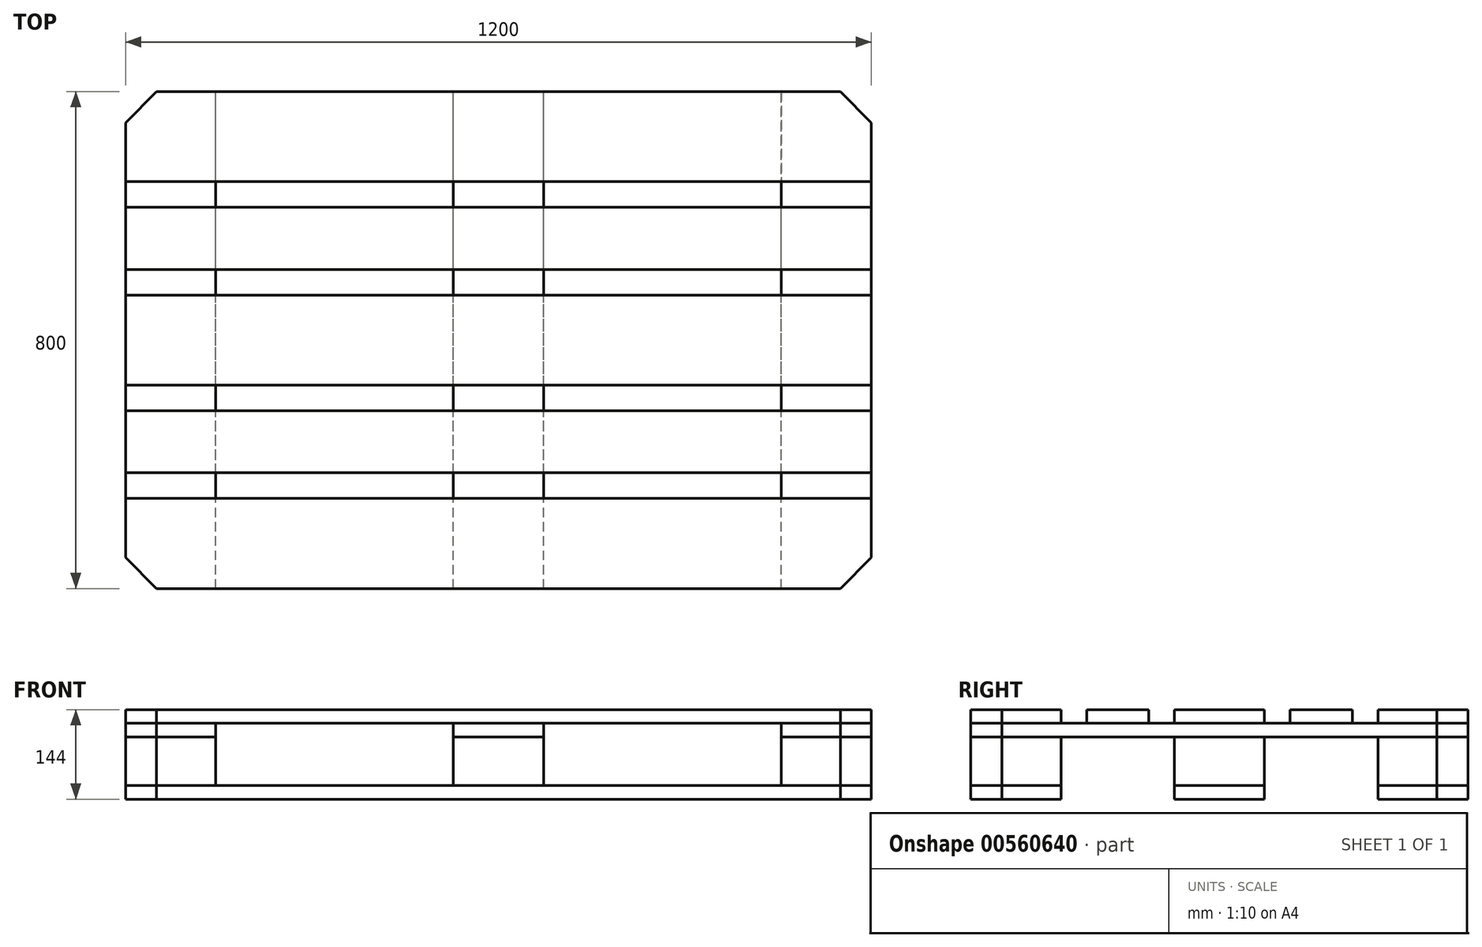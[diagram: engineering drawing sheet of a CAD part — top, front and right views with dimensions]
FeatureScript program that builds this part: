
annotation { "Feature Type Name" : "Feature", "Feature Type Description" : "" }
export const myFeature = defineFeature(function(context is Context, id is Id, definition is map)
    precondition{}
    {
        {
            var Q0;
            Q0=qCreatedBy(makeId("Top.planeOp"),FACE);
            var sketch = newSketch(context, id + "F0", { "sketchPlane" : qUnion([Q0])});
            skLineSegment(sketch, "E0.bottom", {"start": v(600, -72.5) * mm, "end": v(-600, -72.5) * mm});
            skLineSegment(sketch, "E0.top", {"start": v(600, 72.5) * mm, "end": v(-600, 72.5) * mm});
            skLineSegment(sketch, "E0.left", {"start": v(600, -72.5) * mm, "end": v(600, 72.5) * mm});
            skLineSegment(sketch, "E0.right", {"start": v(-600, -72.5) * mm, "end": v(-600, 72.5) * mm});
            skPoint(sketch, "E0.middle", {"position": v(0, 0) * mm});
            skLineSegment(sketch, "E1.bottom", {"start": v(600, -213.75) * mm, "end": v(-600, -213.75) * mm});
            skLineSegment(sketch, "E1.top", {"start": v(600, -113.75) * mm, "end": v(-600, -113.75) * mm});
            skLineSegment(sketch, "E1.left", {"start": v(600, -213.75) * mm, "end": v(600, -113.75) * mm});
            skLineSegment(sketch, "E1.right", {"start": v(-600, -213.75) * mm, "end": v(-600, -113.75) * mm});
            skPoint(sketch, "E1.middle", {"position": v(0, -163.75) * mm});
            skLineSegment(sketch, "E2.bottom", {"start": v(600, -400) * mm, "end": v(-600, -400) * mm});
            skLineSegment(sketch, "E2.top", {"start": v(600, -255) * mm, "end": v(-600, -255) * mm});
            skLineSegment(sketch, "E2.left", {"start": v(600, -400) * mm, "end": v(600, -255) * mm});
            skLineSegment(sketch, "E2.right", {"start": v(-600, -400) * mm, "end": v(-600, -255) * mm});
            skPoint(sketch, "E2.middle", {"position": v(0, -327.5) * mm});
            skLineSegment(sketch, "E3.bottom", {"start": v(-600, 213.75) * mm, "end": v(600, 213.75) * mm});
            skLineSegment(sketch, "E3.top", {"start": v(-600, 113.75) * mm, "end": v(600, 113.75) * mm});
            skLineSegment(sketch, "E3.left", {"start": v(-600, 213.75) * mm, "end": v(-600, 113.75) * mm});
            skLineSegment(sketch, "E3.right", {"start": v(600, 213.75) * mm, "end": v(600, 113.75) * mm});
            skPoint(sketch, "E3.middle", {"position": v(0, 163.75) * mm});
            skLineSegment(sketch, "E4.bottom", {"start": v(-600, 400) * mm, "end": v(600, 400) * mm});
            skLineSegment(sketch, "E4.top", {"start": v(-600, 255) * mm, "end": v(600, 255) * mm});
            skLineSegment(sketch, "E4.left", {"start": v(-600, 400) * mm, "end": v(-600, 255) * mm});
            skLineSegment(sketch, "E4.right", {"start": v(600, 400) * mm, "end": v(600, 255) * mm});
            skPoint(sketch, "E4.middle", {"position": v(0, 327.5) * mm});
            skLineSegment(sketch, "E5", {"start": v(-600, 163.75) * mm, "end": v(600, 163.75) * mm, "construction": true});
            skSolve(sketch);
        }
        {
            var Q0;
            Q0=makeQuery(id+"F0.imprint","IMPRINT",FACE,{"disambiguationData":[TD([[makeQuery(id+"F0.imprint","IMPRINT",EDGE,{"derivedFrom":sQuery(id+"F0.wireOp",EDGE,"E4.bottom")}),-1.0]])]});
            var Q1;
            Q1=makeQuery(id+"F0.imprint","IMPRINT",FACE,{"disambiguationData":[TD([[makeQuery(id+"F0.imprint","IMPRINT",EDGE,{"derivedFrom":sQuery(id+"F0.wireOp",EDGE,"E3.bottom")}),-1.0]])]});
            var Q2;
            Q2=makeQuery(id+"F0.imprint","IMPRINT",FACE,{"disambiguationData":[TD([[makeQuery(id+"F0.imprint","IMPRINT",EDGE,{"derivedFrom":sQuery(id+"F0.wireOp",EDGE,"E0.bottom")}),-1.0]])]});
            var Q3;
            Q3=makeQuery(id+"F0.imprint","IMPRINT",FACE,{"disambiguationData":[TD([[makeQuery(id+"F0.imprint","IMPRINT",EDGE,{"derivedFrom":sQuery(id+"F0.wireOp",EDGE,"E1.bottom")}),-1.0]])]});
            var Q4;
            Q4=makeQuery(id+"F0.imprint","IMPRINT",FACE,{"disambiguationData":[TD([[makeQuery(id+"F0.imprint","IMPRINT",EDGE,{"derivedFrom":sQuery(id+"F0.wireOp",EDGE,"E2.bottom")}),-1.0]])]});
            extrude(context, id + "F1", {"entities" : qUnion([Q0, Q1, Q2, Q3, Q4]), "oppositeDirection" : true, "depth" : 22 * mm, "offsetDistance" : 25 * mm});
        }
        {
            var Q0;
            Q0=makeQuery(id+"F1.opExtrude","CAP_FACE",FACE,{"disambiguationData":[OSD([sQuery(id+"F0.wireOp",EDGE,"E2.bottom"),sQuery(id+"F0.wireOp",EDGE,"E2.top"),sQuery(id+"F0.wireOp",EDGE,"E2.left"),sQuery(id+"F0.wireOp",EDGE,"E2.right")])],"isStart":false});
            var sketch = newSketch(context, id + "F2", { "sketchPlane" : qUnion([Q0])});
            skLineSegment(sketch, "E6.bottom", {"start": v(-600, 400) * mm, "end": v(-455, 400) * mm});
            skLineSegment(sketch, "E6.top", {"start": v(-600, -400) * mm, "end": v(-455, -400) * mm});
            skLineSegment(sketch, "E6.left", {"start": v(-600, 400) * mm, "end": v(-600, -400) * mm});
            skLineSegment(sketch, "E6.right", {"start": v(-455, 400) * mm, "end": v(-455, -400) * mm});
            skLineSegment(sketch, "E7.bottom", {"start": v(-72.5, 400) * mm, "end": v(72.5, 400) * mm});
            skLineSegment(sketch, "E7.top", {"start": v(-72.5, -400) * mm, "end": v(72.5, -400) * mm});
            skLineSegment(sketch, "E7.left", {"start": v(-72.5, 400) * mm, "end": v(-72.5, -400) * mm});
            skLineSegment(sketch, "E7.right", {"start": v(72.5, 400) * mm, "end": v(72.5, -400) * mm});
            skLineSegment(sketch, "E8.bottom", {"start": v(600, 400) * mm, "end": v(455, 400) * mm});
            skLineSegment(sketch, "E8.top", {"start": v(600, -400) * mm, "end": v(455, -400) * mm});
            skLineSegment(sketch, "E8.left", {"start": v(600, 400) * mm, "end": v(600, -400) * mm});
            skLineSegment(sketch, "E8.right", {"start": v(455, 400) * mm, "end": v(455, -400) * mm});
            skSolve(sketch);
        }
        {
            var Q0;
            {var subQ0=sQuery(id+"F2.wireOp",EDGE,"E6.top");Q0=makeQuery(id+"F2.imprint","IMPRINT",FACE,{"disambiguationData":[TD([[makeQuery(id+"F2.imprint","IMPRINT",EDGE,{"derivedFrom":subQ0}),1.0]])]});}
            var Q1;
            {var subQ0=sQuery(id+"F2.wireOp",EDGE,"E6.bottom");Q1=makeQuery(id+"F2.imprint","IMPRINT",FACE,{"disambiguationData":[TD([[makeQuery(id+"F2.imprint","IMPRINT",EDGE,{"derivedFrom":subQ0}),1.0]])]});}
            var Q2;
            {var subQ0=sQuery(id+"F2.wireOp",EDGE,"E7.bottom");Q2=makeQuery(id+"F2.imprint","IMPRINT",FACE,{"disambiguationData":[TD([[makeQuery(id+"F2.imprint","IMPRINT",EDGE,{"derivedFrom":subQ0}),1.0]])]});}
            var Q3;
            {var subQ0=sQuery(id+"F2.wireOp",EDGE,"E7.top");Q3=makeQuery(id+"F2.imprint","IMPRINT",FACE,{"disambiguationData":[TD([[makeQuery(id+"F2.imprint","IMPRINT",EDGE,{"derivedFrom":subQ0}),1.0]])]});}
            var Q4;
            {var subQ0=sQuery(id+"F2.wireOp",EDGE,"E8.bottom");Q4=makeQuery(id+"F2.imprint","IMPRINT",FACE,{"disambiguationData":[TD([[makeQuery(id+"F2.imprint","IMPRINT",EDGE,{"derivedFrom":subQ0}),1.0]])]});}
            var Q5;
            {var subQ0=sQuery(id+"F2.wireOp",EDGE,"E8.top");Q5=makeQuery(id+"F2.imprint","IMPRINT",FACE,{"disambiguationData":[TD([[makeQuery(id+"F2.imprint","IMPRINT",EDGE,{"derivedFrom":subQ0}),-1.0]])]});}
            extrude(context, id + "F3", {"entities" : qUnion([Q0, Q1, Q2, Q3, Q4, Q5]), "depth" : 22 * mm, "offsetDistance" : 25 * mm});
        }
        {
            var Q0;
            Q0=makeQuery(id+"F3.opExtrude","CAP_FACE",FACE,{"disambiguationData":[OSD([sQuery(id+"F2.wireOp",EDGE,"E6.bottom"),sQuery(id+"F2.wireOp",EDGE,"E6.top"),sQuery(id+"F2.wireOp",EDGE,"E6.left"),sQuery(id+"F2.wireOp",EDGE,"E6.right")])],"isStart":false});
            var sketch = newSketch(context, id + "F4", { "sketchPlane" : qUnion([Q0])});
            skLineSegment(sketch, "E9.bottom", {"start": v(-600, 400) * mm, "end": v(-455, 400) * mm});
            skLineSegment(sketch, "E9.top", {"start": v(-600, 255) * mm, "end": v(-455, 255) * mm});
            skLineSegment(sketch, "E9.left", {"start": v(-600, 400) * mm, "end": v(-600, 255) * mm});
            skLineSegment(sketch, "E9.right", {"start": v(-455, 400) * mm, "end": v(-455, 255) * mm});
            skLineSegment(sketch, "E10.bottom", {"start": v(-600, 72.5) * mm, "end": v(-455, 72.5) * mm});
            skLineSegment(sketch, "E10.top", {"start": v(-600, -72.5) * mm, "end": v(-455, -72.5) * mm});
            skLineSegment(sketch, "E10.left", {"start": v(-600, 72.5) * mm, "end": v(-600, -72.5) * mm});
            skLineSegment(sketch, "E10.right", {"start": v(-455, 72.5) * mm, "end": v(-455, -72.5) * mm});
            skLineSegment(sketch, "E11.bottom", {"start": v(-600, -400) * mm, "end": v(-455, -400) * mm});
            skLineSegment(sketch, "E11.top", {"start": v(-600, -255) * mm, "end": v(-455, -255) * mm});
            skLineSegment(sketch, "E11.left", {"start": v(-600, -400) * mm, "end": v(-600, -255) * mm});
            skLineSegment(sketch, "E11.right", {"start": v(-455, -400) * mm, "end": v(-455, -255) * mm});
            skLineSegment(sketch, "E12.1.0.0", {"start": v(-72.5, 72.5) * mm, "end": v(-72.5, -72.5) * mm});
            skLineSegment(sketch, "E12.1.0.1", {"start": v(-72.5, -72.5) * mm, "end": v(72.5, -72.5) * mm});
            skLineSegment(sketch, "E12.1.0.2", {"start": v(-72.5, 72.5) * mm, "end": v(72.5, 72.5) * mm});
            skLineSegment(sketch, "E12.1.0.3", {"start": v(72.5, 400) * mm, "end": v(72.5, 255) * mm});
            skLineSegment(sketch, "E12.1.0.4", {"start": v(-72.5, 400) * mm, "end": v(-72.5, 255) * mm});
            skLineSegment(sketch, "E12.1.0.5", {"start": v(72.5, 72.5) * mm, "end": v(72.5, -72.5) * mm});
            skLineSegment(sketch, "E12.1.0.6", {"start": v(-72.5, 255) * mm, "end": v(72.5, 255) * mm});
            skLineSegment(sketch, "E12.1.0.7", {"start": v(72.5, -400) * mm, "end": v(72.5, -255) * mm});
            skLineSegment(sketch, "E12.1.0.8", {"start": v(-72.5, 400) * mm, "end": v(72.5, 400) * mm});
            skLineSegment(sketch, "E12.1.0.9", {"start": v(-72.5, -400) * mm, "end": v(72.5, -400) * mm});
            skLineSegment(sketch, "E12.1.0.10", {"start": v(-72.5, -255) * mm, "end": v(72.5, -255) * mm});
            skLineSegment(sketch, "E12.1.0.11", {"start": v(-72.5, -400) * mm, "end": v(-72.5, -255) * mm});
            skLineSegment(sketch, "E12.2.0.0", {"start": v(455, 72.5) * mm, "end": v(455, -72.5) * mm});
            skLineSegment(sketch, "E12.2.0.1", {"start": v(455, -72.5) * mm, "end": v(600, -72.5) * mm});
            skLineSegment(sketch, "E12.2.0.2", {"start": v(455, 72.5) * mm, "end": v(600, 72.5) * mm});
            skLineSegment(sketch, "E12.2.0.3", {"start": v(600, 400) * mm, "end": v(600, 255) * mm});
            skLineSegment(sketch, "E12.2.0.4", {"start": v(455, 400) * mm, "end": v(455, 255) * mm});
            skLineSegment(sketch, "E12.2.0.5", {"start": v(600, 72.5) * mm, "end": v(600, -72.5) * mm});
            skLineSegment(sketch, "E12.2.0.6", {"start": v(455, 255) * mm, "end": v(600, 255) * mm});
            skLineSegment(sketch, "E12.2.0.7", {"start": v(600, -400) * mm, "end": v(600, -255) * mm});
            skLineSegment(sketch, "E12.2.0.8", {"start": v(455, 400) * mm, "end": v(600, 400) * mm});
            skLineSegment(sketch, "E12.2.0.9", {"start": v(455, -400) * mm, "end": v(600, -400) * mm});
            skLineSegment(sketch, "E12.2.0.10", {"start": v(455, -255) * mm, "end": v(600, -255) * mm});
            skLineSegment(sketch, "E12.2.0.11", {"start": v(455, -400) * mm, "end": v(455, -255) * mm});
            skLineSegment(sketch, "E12.direction1", {"start": v(-600, -400) * mm, "end": v(-72.5, -400) * mm, "construction": true});
            skSolve(sketch);
        }
        {
            var Q0;
            Q0=makeQuery(id+"F4.imprint","IMPRINT",FACE,{"disambiguationData":[TD([[makeQuery(id+"F4.imprint","IMPRINT",EDGE,{"derivedFrom":sQuery(id+"F4.wireOp",EDGE,"E9.bottom")}),1.0]])]});
            var Q1;
            Q1=makeQuery(id+"F4.imprint","IMPRINT",FACE,{"disambiguationData":[TD([[makeQuery(id+"F4.imprint","IMPRINT",EDGE,{"derivedFrom":sQuery(id+"F4.wireOp",EDGE,"E10.bottom")}),-1.0]])]});
            var Q2;
            Q2=makeQuery(id+"F4.imprint","IMPRINT",FACE,{"disambiguationData":[TD([[makeQuery(id+"F4.imprint","IMPRINT",EDGE,{"derivedFrom":sQuery(id+"F4.wireOp",EDGE,"E11.bottom")}),1.0]])]});
            var Q3;
            Q3=makeQuery(id+"F4.imprint","IMPRINT",FACE,{"disambiguationData":[TD([[makeQuery(id+"F4.imprint","IMPRINT",EDGE,{"derivedFrom":sQuery(id+"F4.wireOp",EDGE,"E12.1.0.7")}),1.0]])]});
            var Q4;
            Q4=makeQuery(id+"F4.imprint","IMPRINT",FACE,{"disambiguationData":[TD([[makeQuery(id+"F4.imprint","IMPRINT",EDGE,{"derivedFrom":sQuery(id+"F4.wireOp",EDGE,"E12.1.0.0")}),1.0]])]});
            var Q5;
            Q5=makeQuery(id+"F4.imprint","IMPRINT",FACE,{"disambiguationData":[TD([[makeQuery(id+"F4.imprint","IMPRINT",EDGE,{"derivedFrom":sQuery(id+"F4.wireOp",EDGE,"E12.1.0.3")}),-1.0]])]});
            var Q6;
            Q6=makeQuery(id+"F4.imprint","IMPRINT",FACE,{"disambiguationData":[TD([[makeQuery(id+"F4.imprint","IMPRINT",EDGE,{"derivedFrom":sQuery(id+"F4.wireOp",EDGE,"E12.2.0.3")}),-1.0]])]});
            var Q7;
            Q7=makeQuery(id+"F4.imprint","IMPRINT",FACE,{"disambiguationData":[TD([[makeQuery(id+"F4.imprint","IMPRINT",EDGE,{"derivedFrom":sQuery(id+"F4.wireOp",EDGE,"E12.2.0.0")}),1.0]])]});
            var Q8;
            Q8=makeQuery(id+"F4.imprint","IMPRINT",FACE,{"disambiguationData":[TD([[makeQuery(id+"F4.imprint","IMPRINT",EDGE,{"derivedFrom":sQuery(id+"F4.wireOp",EDGE,"E12.2.0.7")}),1.0]])]});
            extrude(context, id + "F5", {"entities" : qUnion([Q0, Q1, Q2, Q3, Q4, Q5, Q6, Q7, Q8]), "depth" : 78 * mm, "offsetDistance" : 25 * mm});
        }
        {
            var Q0;
            Q0=makeQuery(id+"F5.opExtrude","CAP_FACE",FACE,{"disambiguationData":[OSD([sQuery(id+"F4.wireOp",EDGE,"E9.bottom"),sQuery(id+"F4.wireOp",EDGE,"E9.top"),sQuery(id+"F4.wireOp",EDGE,"E9.left"),sQuery(id+"F4.wireOp",EDGE,"E9.right")])],"isStart":false});
            var sketch = newSketch(context, id + "F6", { "sketchPlane" : qUnion([Q0])});
            skLineSegment(sketch, "E13.bottom", {"start": v(-600, 400) * mm, "end": v(600, 400) * mm});
            skLineSegment(sketch, "E13.top", {"start": v(-600, 255) * mm, "end": v(600, 255) * mm});
            skLineSegment(sketch, "E13.left", {"start": v(-600, 400) * mm, "end": v(-600, 255) * mm});
            skLineSegment(sketch, "E13.right", {"start": v(600, 400) * mm, "end": v(600, 255) * mm});
            skLineSegment(sketch, "E14.bottom", {"start": v(-600, 72.5) * mm, "end": v(600, 72.5) * mm});
            skLineSegment(sketch, "E14.top", {"start": v(-600, -72.5) * mm, "end": v(600, -72.5) * mm});
            skLineSegment(sketch, "E14.left", {"start": v(-600, 72.5) * mm, "end": v(-600, -72.5) * mm});
            skLineSegment(sketch, "E14.right", {"start": v(600, 72.5) * mm, "end": v(600, -72.5) * mm});
            skLineSegment(sketch, "E15.bottom", {"start": v(-600, -255) * mm, "end": v(600, -255) * mm});
            skLineSegment(sketch, "E15.top", {"start": v(-600, -400) * mm, "end": v(600, -400) * mm});
            skLineSegment(sketch, "E15.left", {"start": v(-600, -255) * mm, "end": v(-600, -400) * mm});
            skLineSegment(sketch, "E15.right", {"start": v(600, -255) * mm, "end": v(600, -400) * mm});
            skSolve(sketch);
        }
        {
            var Q0;
            {var subQ0=sQuery(id+"F6.wireOp",EDGE,"E13.left");Q0=makeQuery(id+"F6.imprint","IMPRINT",FACE,{"disambiguationData":[TD([[makeQuery(id+"F6.imprint","IMPRINT",EDGE,{"derivedFrom":subQ0}),1.0]])]});}
            var Q1;
            {var subQ2=sQuery(id+"F6.wireOp",EDGE,"E13.right");Q1=makeQuery(id+"F6.imprint","IMPRINT",FACE,{"disambiguationData":[TD([[makeQuery(id+"F6.imprint","IMPRINT",EDGE,{"derivedFrom":subQ2}),-1.0]])]});}
            var Q2;
            Q2=makeQuery(id+"F6.imprint","IMPRINT",FACE,{"disambiguationData":[TD([[makeQuery(id+"F6.imprint","IMPRINT",EDGE,{"derivedFrom":sQuery(id+"F6.wireOp",EDGE,"E14.bottom")}),-1.0]])]});
            var Q3;
            Q3=makeQuery(id+"F6.imprint","IMPRINT",FACE,{"disambiguationData":[TD([[makeQuery(id+"F6.imprint","IMPRINT",EDGE,{"derivedFrom":sQuery(id+"F6.wireOp",EDGE,"E15.bottom")}),-1.0]])]});
            extrude(context, id + "F7", {"entities" : qUnion([Q0, Q1, Q2, Q3]), "depth" : 22 * mm, "offsetDistance" : 25 * mm});
        }
        {
            var Q0;
            Q0=makeQuery(id+"F1.opExtrude","SWEPT_EDGE",EDGE,{"disambiguationData":[OSD([sQuery(id+"F0.wireOp",EDGE,"E2.bottom"),sQuery(id+"F0.wireOp",EDGE,"E2.right")])]});
            var Q1;
            Q1=makeQuery(id+"F3.opExtrude","SWEPT_EDGE",EDGE,{"disambiguationData":[OSD([sQuery(id+"F2.wireOp",EDGE,"E6.bottom"),sQuery(id+"F2.wireOp",EDGE,"E6.left")])]});
            var Q2;
            Q2=makeQuery(id+"F5.opExtrude","SWEPT_EDGE",EDGE,{"disambiguationData":[OSD([sQuery(id+"F4.wireOp",EDGE,"E9.bottom"),sQuery(id+"F4.wireOp",EDGE,"E9.left")])]});
            var Q3;
            Q3=makeQuery(id+"F7.opExtrude","SWEPT_EDGE",EDGE,{"disambiguationData":[OSD([sQuery(id+"F6.wireOp",EDGE,"E13.bottom"),sQuery(id+"F6.wireOp",EDGE,"E13.left")])]});
            var Q4;
            Q4=makeQuery(id+"F1.opExtrude","SWEPT_EDGE",EDGE,{"disambiguationData":[OSD([sQuery(id+"F0.wireOp",EDGE,"E2.bottom"),sQuery(id+"F0.wireOp",EDGE,"E2.left")])]});
            var Q5;
            Q5=makeQuery(id+"F3.opExtrude","SWEPT_EDGE",EDGE,{"disambiguationData":[OSD([sQuery(id+"F2.wireOp",EDGE,"E8.bottom"),sQuery(id+"F2.wireOp",EDGE,"E8.left")])]});
            var Q6;
            Q6=makeQuery(id+"F5.opExtrude","SWEPT_EDGE",EDGE,{"disambiguationData":[OSD([sQuery(id+"F4.wireOp",EDGE,"E12.2.0.3"),sQuery(id+"F4.wireOp",EDGE,"E12.2.0.8")])]});
            var Q7;
            Q7=makeQuery(id+"F7.opExtrude","SWEPT_EDGE",EDGE,{"disambiguationData":[OSD([sQuery(id+"F6.wireOp",EDGE,"E13.bottom"),sQuery(id+"F6.wireOp",EDGE,"E13.right")])]});
            var Q8;
            Q8=makeQuery(id+"F1.opExtrude","SWEPT_EDGE",EDGE,{"disambiguationData":[OSD([sQuery(id+"F0.wireOp",EDGE,"E4.bottom"),sQuery(id+"F0.wireOp",EDGE,"E4.right")])]});
            var Q9;
            Q9=makeQuery(id+"F3.opExtrude","SWEPT_EDGE",EDGE,{"disambiguationData":[OSD([sQuery(id+"F2.wireOp",EDGE,"E8.top"),sQuery(id+"F2.wireOp",EDGE,"E8.left")])]});
            var Q10;
            Q10=makeQuery(id+"F5.opExtrude","SWEPT_EDGE",EDGE,{"disambiguationData":[OSD([sQuery(id+"F4.wireOp",EDGE,"E12.2.0.7"),sQuery(id+"F4.wireOp",EDGE,"E12.2.0.9")])]});
            var Q11;
            Q11=makeQuery(id+"F7.opExtrude","SWEPT_EDGE",EDGE,{"disambiguationData":[OSD([sQuery(id+"F6.wireOp",EDGE,"E15.top"),sQuery(id+"F6.wireOp",EDGE,"E15.right")])]});
            var Q12;
            Q12=makeQuery(id+"F1.opExtrude","SWEPT_EDGE",EDGE,{"disambiguationData":[OSD([sQuery(id+"F0.wireOp",EDGE,"E4.bottom"),sQuery(id+"F0.wireOp",EDGE,"E4.left")])]});
            var Q13;
            Q13=makeQuery(id+"F3.opExtrude","SWEPT_EDGE",EDGE,{"disambiguationData":[OSD([sQuery(id+"F2.wireOp",EDGE,"E6.top"),sQuery(id+"F2.wireOp",EDGE,"E6.left")])]});
            var Q14;
            Q14=makeQuery(id+"F5.opExtrude","SWEPT_EDGE",EDGE,{"disambiguationData":[OSD([sQuery(id+"F4.wireOp",EDGE,"E11.bottom"),sQuery(id+"F4.wireOp",EDGE,"E11.left")])]});
            var Q15;
            Q15=makeQuery(id+"F7.opExtrude","SWEPT_EDGE",EDGE,{"disambiguationData":[OSD([sQuery(id+"F6.wireOp",EDGE,"E15.top"),sQuery(id+"F6.wireOp",EDGE,"E15.left")])]});
            chamfer(context, id + "F8", {"entities" : qUnion([Q0, Q1, Q2, Q3, Q4, Q5, Q6, Q7, Q8, Q9, Q10, Q11, Q12, Q13, Q14, Q15]), "width" : 50 * mm, "tangentPropagation" : true});
        }
    });
